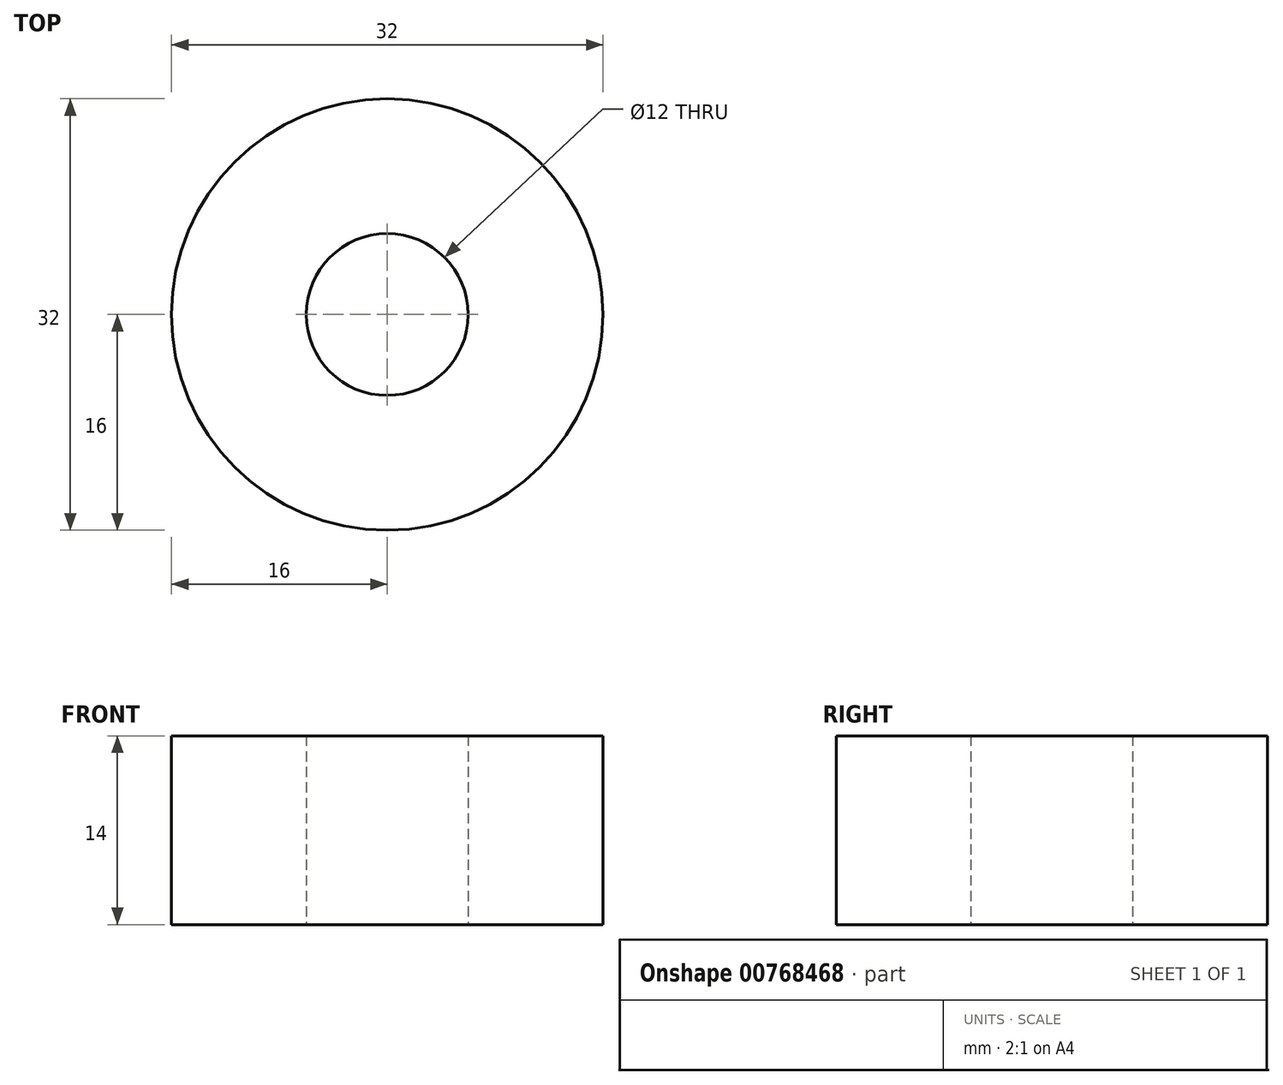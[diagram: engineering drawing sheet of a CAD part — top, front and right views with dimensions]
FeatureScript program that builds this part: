
annotation { "Feature Type Name" : "Feature", "Feature Type Description" : "" }
export const myFeature = defineFeature(function(context is Context, id is Id, definition is map)
    precondition{}
    {
        {
            var Q0;
            Q0=qCreatedBy(makeId("Top.planeOp"),FACE);
            var sketch = newSketch(context, id + "F0", { "sketchPlane" : qUnion([Q0])});
            skCircle(sketch, "E0", {"center": v(0, 0) * mm, "radius": 6 * mm});
            skCircle(sketch, "E1", {"center": v(0, 0) * mm, "radius": 16 * mm});
            skSolve(sketch);
        }
        {
            var Q0;
            Q0=makeQuery(id+"F0.imprint","IMPRINT",FACE,{"disambiguationData":[TD([[makeQuery(id+"F0.imprint","IMPRINT",EDGE,{"derivedFrom":sQuery(id+"F0.wireOp",EDGE,"E0")}),-1.0]])]});
            extrude(context, id + "F1", {"entities" : qUnion([Q0]), "depth" : 14 * mm, "offsetDistance" : 25 * mm});
        }
    });
